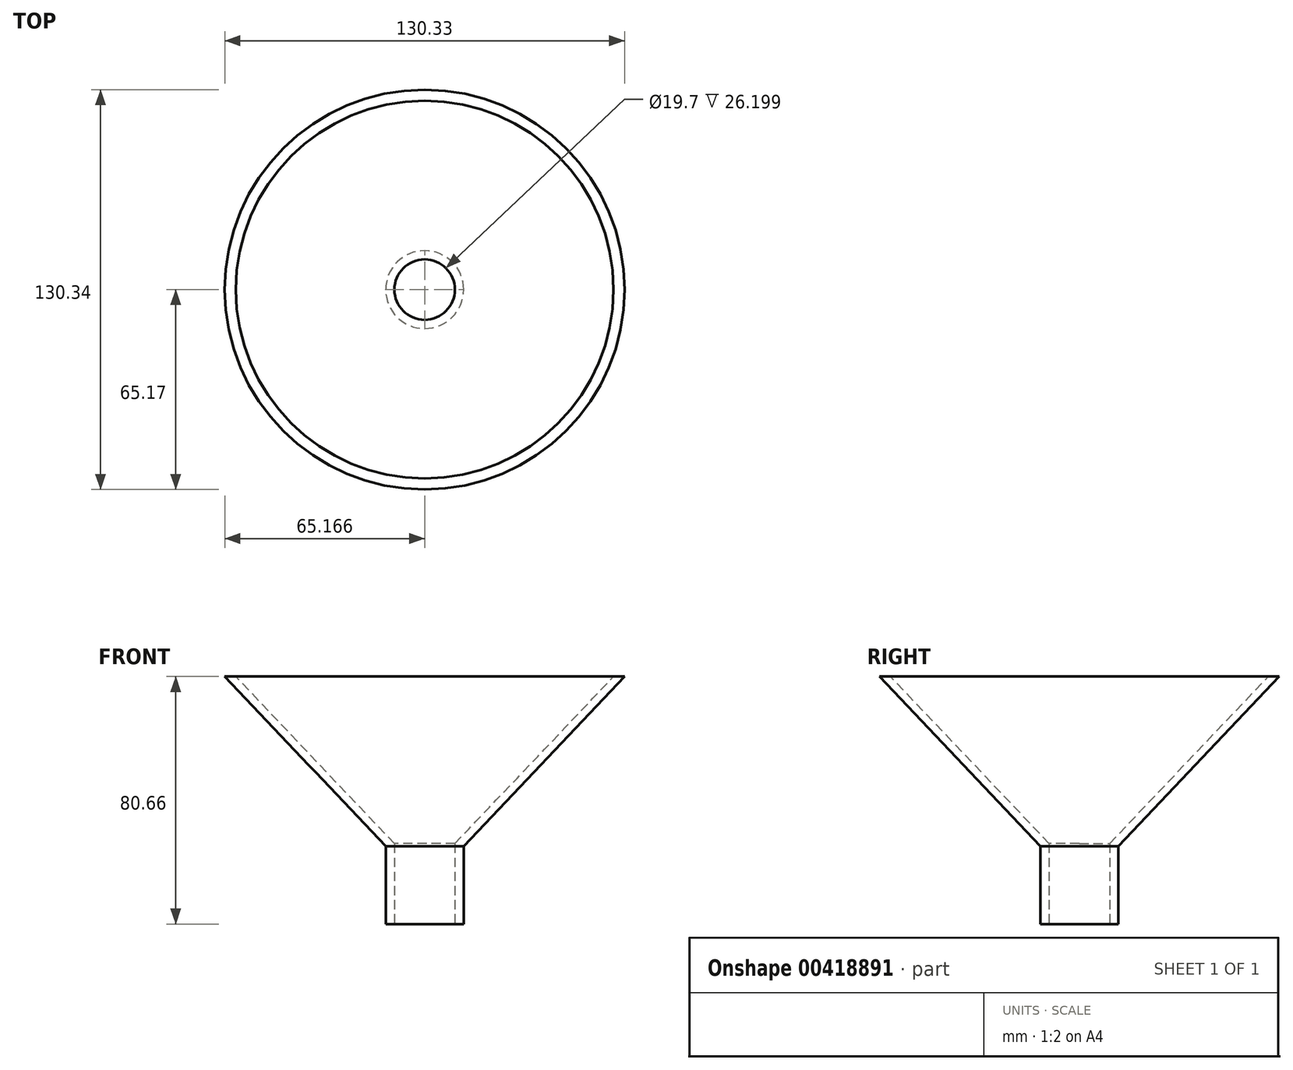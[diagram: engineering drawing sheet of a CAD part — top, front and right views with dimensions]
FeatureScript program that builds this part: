
annotation { "Feature Type Name" : "Feature", "Feature Type Description" : "" }
export const myFeature = defineFeature(function(context is Context, id is Id, definition is map)
    precondition{}
    {
        {
            var Q0;
            Q0=qCreatedBy(makeId("Front.planeOp"),FACE);
            var sketch = newSketch(context, id + "F0", { "sketchPlane" : qUnion([Q0])});
            skLineSegment(sketch, "E0", {"start": v(59.16, 68.39) * mm, "end": v(6.7, 13.13) * mm});
            skLineSegment(sketch, "E1", {"start": v(6.7, 13.13) * mm, "end": v(6.7, -12.27) * mm});
            skLineSegment(sketch, "E2", {"start": v(6.7, -12.27) * mm, "end": v(-6, -12.27) * mm});
            skLineSegment(sketch, "E3", {"start": v(-6, -12.27) * mm, "end": v(-6, 13.13) * mm});
            skLineSegment(sketch, "E4", {"start": v(-6, 13.13) * mm, "end": v(3.09, 13.13) * mm});
            skLineSegment(sketch, "E5", {"start": v(3.09, 13.13) * mm, "end": v(55.56, 68.39) * mm});
            skLineSegment(sketch, "E6", {"start": v(55.56, 68.39) * mm, "end": v(59.16, 68.39) * mm});
            skSolve(sketch);
        }
        {
            var Q0;
            Q0 = qSketchRegion(id + "F0", true);
            var Q1;
            Q1=makeQuery(id+"F0.imprint","IMPRINT",FACE,{"disambiguationData":[TD([[makeQuery(id+"F0.imprint","IMPRINT",EDGE,{"derivedFrom":sQuery(id+"F0.wireOp",EDGE,"E0")}),-1.0]])]});
            var Q2;
            Q2=sQuery(id+"F0.wireOp",EDGE,"E3");
            revolve(context, id + "F1", {"entities" : qUnion([Q0, Q1]), "axis" : qUnion([Q2]), "revolveType" : RevolveType.FULL});
        }
        {
            var Q0;
            Q0=makeQuery(id+"F1.opRevolve","SWEPT_FACE",FACE,{"disambiguationData":[OSD([sQuery(id+"F0.wireOp",EDGE,"E2")])]});
            var sketch = newSketch(context, id + "F2", { "sketchPlane" : qUnion([Q0])});
            skCircle(sketch, "E7", {"center": v(-6, 0) * mm, "radius": 9.85 * mm});
            skSolve(sketch);
        }
        {
            var Q0;
            Q0=makeQuery(id+"F2.imprint","IMPRINT",FACE,{"disambiguationData":[TD([[makeQuery(id+"F2.imprint","IMPRINT",EDGE,{"derivedFrom":sQuery(id+"F2.wireOp",EDGE,"E7")}),1.0]])]});
            extrude(context, id + "F3", {"entities" : qUnion([Q0]), "operationType" : NewBodyOperationType.REMOVE, "oppositeDirection" : true, "depth" : 50.8 * mm});
        }
    });
